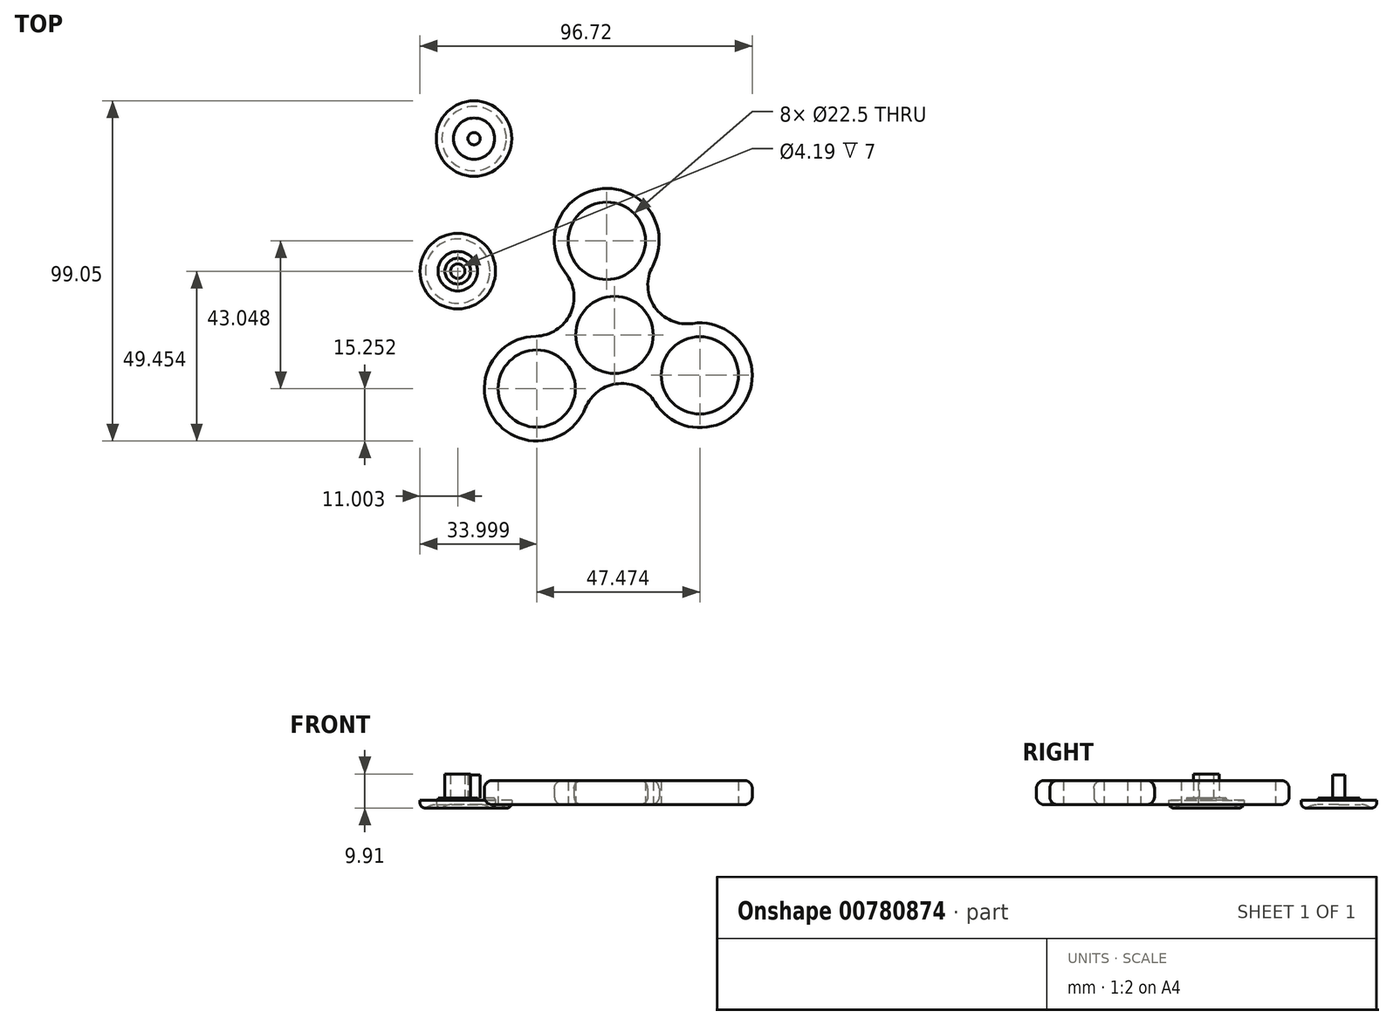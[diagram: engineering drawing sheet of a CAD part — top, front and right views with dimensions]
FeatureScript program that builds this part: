
annotation { "Feature Type Name" : "Feature", "Feature Type Description" : "" }
export const myFeature = defineFeature(function(context is Context, id is Id, definition is map)
    precondition{}
    {
        {
            var Q0;
            Q0=qCreatedBy(makeId("Top.planeOp"),FACE);
            var sketch = newSketch(context, id + "F0", { "sketchPlane" : qUnion([Q0])});
            skCircle(sketch, "E0", {"center": v(0, 0) * mm, "radius": 11.25 * mm});
            skCircle(sketch, "E1", {"center": v(-22.62, -15.64) * mm, "radius": 11.25 * mm});
            skCircle(sketch, "E2", {"center": v(24.85, -11.77) * mm, "radius": 11.25 * mm});
            skCircle(sketch, "E3", {"center": v(-2.23, 27.4) * mm, "radius": 11.25 * mm});
            skCircle(sketch, "E4.0", {"center": v(-22.62, -15.64) * mm, "radius": 15.25 * mm});
            skCircle(sketch, "E5.0", {"center": v(-2.23, 27.4) * mm, "radius": 15.25 * mm});
            skCircle(sketch, "E6.0", {"center": v(24.85, -11.77) * mm, "radius": 15.25 * mm});
            skLineSegment(sketch, "E7", {"start": v(-16.1, -1.86) * mm, "end": v(-8.76, 13.63) * mm, "construction": true});
            skLineSegment(sketch, "E8", {"start": v(16.18, 0.77) * mm, "end": v(6.44, 14.87) * mm, "construction": true});
            skLineSegment(sketch, "E9", {"start": v(-7.42, -14.4) * mm, "end": v(9.65, -13) * mm, "construction": true});
            skArc(sketch, "E10", {"start": v(11.8, -19.65) * mm, "mid": v(1.16, -14.2) * mm, "end": v(-8.46, -21.3) * mm});
            skArc(sketch, "E11", {"start": v(-22.92, -0.4) * mm, "mid": v(-12.88, 6.1) * mm, "end": v(-14.22, 17.98) * mm});
            skArc(sketch, "E12", {"start": v(11.12, 20.04) * mm, "mid": v(11.72, 8.1) * mm, "end": v(22.68, 3.32) * mm});
            skSolve(sketch);
        }
        {
            var Q0;
            Q0=makeQuery(id+"F0.imprint","IMPRINT",FACE,{"disambiguationData":[TD([[makeQuery(id+"F0.imprint","IMPRINT",EDGE,{"derivedFrom":sQuery(id+"F0.wireOp",EDGE,"E1")}),-1.0]])]});
            var Q1;
            Q1=makeQuery(id+"F0.imprint","IMPRINT",FACE,{"disambiguationData":[TD([[makeQuery(id+"F0.imprint","IMPRINT",EDGE,{"derivedFrom":sQuery(id+"F0.wireOp",EDGE,"E0")}),-1.0]])]});
            var Q2;
            Q2=makeQuery(id+"F0.imprint","IMPRINT",FACE,{"disambiguationData":[TD([[makeQuery(id+"F0.imprint","IMPRINT",EDGE,{"derivedFrom":sQuery(id+"F0.wireOp",EDGE,"E3")}),-1.0]])]});
            var Q3;
            Q3=makeQuery(id+"F0.imprint","IMPRINT",FACE,{"disambiguationData":[TD([[makeQuery(id+"F0.imprint","IMPRINT",EDGE,{"derivedFrom":sQuery(id+"F0.wireOp",EDGE,"E2")}),-1.0]])]});
            extrude(context, id + "F1", {"entities" : qUnion([Q0, Q1, Q2, Q3]), "depth" : 7 * mm, "offsetDistance" : 25.4 * mm});
        }
        {
            var Q0;
            Q0=makeQuery(id+"F1.opExtrude","CAP_EDGE",EDGE,{"disambiguationData":[OSD([sQuery(id+"F0.wireOp",EDGE,"E4.0")])],"isStart":false});
            fillet(context, id + "F2", {"entities" : qUnion([Q0]), "radius" : 2.3 * mm, "tangentPropagation" : true, "allowEdgeOverflow" : false});
        }
        {
            var Q0;
            Q0=makeQuery(id+"F1.opExtrude","CAP_EDGE",EDGE,{"disambiguationData":[OSD([sQuery(id+"F0.wireOp",EDGE,"E5.0")])],"isStart":true});
            fillet(context, id + "F3", {"entities" : qUnion([Q0]), "radius" : 2.3 * mm, "tangentPropagation" : true, "allowEdgeOverflow" : false});
        }
        {
            var Q0;
            Q0=qCreatedBy(makeId("Top.planeOp"),FACE);
            var sketch = newSketch(context, id + "F4", { "sketchPlane" : qUnion([Q0])});
            skCircle(sketch, "E13", {"center": v(-45.62, 18.56) * mm, "radius": 11 * mm});
            skCircle(sketch, "E14.0", {"center": v(-45.62, 18.56) * mm, "radius": 3.75 * mm});
            skCircle(sketch, "E15.0", {"center": v(-45.62, 18.56) * mm, "radius": 5.75 * mm});
            skCircle(sketch, "E16", {"center": v(-45.62, 18.56) * mm, "radius": 2.1 * mm});
            skSolve(sketch);
        }
        {
            var Q0;
            Q0=makeQuery(id+"F4.imprint","IMPRINT",FACE,{"disambiguationData":[TD([[makeQuery(id+"F4.imprint","IMPRINT",EDGE,{"derivedFrom":sQuery(id+"F4.wireOp",EDGE,"E13")}),1.0]])]});
            extrude(context, id + "F5", {"entities" : qUnion([Q0]), "depth" : 1.27 * mm, "offsetDistance" : 25.4 * mm});
        }
        {
            var Q0;
            Q0=makeQuery(id+"F4.imprint","IMPRINT",FACE,{"disambiguationData":[TD([[makeQuery(id+"F4.imprint","IMPRINT",EDGE,{"derivedFrom":sQuery(id+"F4.wireOp",EDGE,"E14.0")}),-1.0]])]});
            var Q1;
            Q1=makeQuery(id+"F4.imprint","IMPRINT",FACE,{"disambiguationData":[TD([[makeQuery(id+"F4.imprint","IMPRINT",EDGE,{"derivedFrom":sQuery(id+"F4.wireOp",EDGE,"E16")}),1.0]])]});
            extrude(context, id + "F6", {"entities" : qUnion([Q0, Q1]), "operationType" : NewBodyOperationType.ADD, "depth" : 1.9 * mm, "offsetDistance" : 25.4 * mm});
        }
        {
            var Q0;
            Q0=makeQuery(id+"F4.imprint","IMPRINT",FACE,{"disambiguationData":[TD([[makeQuery(id+"F4.imprint","IMPRINT",EDGE,{"derivedFrom":sQuery(id+"F4.wireOp",EDGE,"E14.0")}),1.0]])]});
            extrude(context, id + "F7", {"entities" : qUnion([Q0]), "operationType" : NewBodyOperationType.ADD, "depth" : 8.9 * mm, "offsetDistance" : 25.4 * mm});
        }
        {
            var Q0;
            Q0=qCreatedBy(makeId("Top.planeOp"),FACE);
            var sketch = newSketch(context, id + "F8", { "sketchPlane" : qUnion([Q0])});
            skCircle(sketch, "E17", {"center": v(-40.87, 57.16) * mm, "radius": 11 * mm});
            skCircle(sketch, "E18", {"center": v(-40.87, 57.16) * mm, "radius": 6 * mm});
            skCircle(sketch, "E19", {"center": v(-40.87, 57.16) * mm, "radius": 1.78 * mm});
            skSolve(sketch);
        }
        {
            var Q0;
            Q0=makeQuery(id+"F8.imprint","IMPRINT",FACE,{"disambiguationData":[TD([[makeQuery(id+"F8.imprint","IMPRINT",EDGE,{"derivedFrom":sQuery(id+"F8.wireOp",EDGE,"E17")}),1.0]])]});
            extrude(context, id + "F9", {"entities" : qUnion([Q0]), "depth" : 1.27 * mm, "offsetDistance" : 25.4 * mm});
        }
        {
            var Q0;
            Q0=makeQuery(id+"F8.imprint","IMPRINT",FACE,{"disambiguationData":[TD([[makeQuery(id+"F8.imprint","IMPRINT",EDGE,{"derivedFrom":sQuery(id+"F8.wireOp",EDGE,"E18")}),1.0]])]});
            extrude(context, id + "F10", {"entities" : qUnion([Q0]), "operationType" : NewBodyOperationType.ADD, "depth" : 1.9 * mm, "offsetDistance" : 25.4 * mm});
        }
        {
            var Q0;
            Q0=makeQuery(id+"F8.imprint","IMPRINT",FACE,{"disambiguationData":[TD([[makeQuery(id+"F8.imprint","IMPRINT",EDGE,{"derivedFrom":sQuery(id+"F8.wireOp",EDGE,"E19")}),1.0]])]});
            extrude(context, id + "F11", {"entities" : qUnion([Q0]), "operationType" : NewBodyOperationType.ADD, "depth" : 8.65 * mm, "offsetDistance" : 25.4 * mm});
        }
        {
            var Q0;
            Q0=makeQuery(id+"F8.imprint","IMPRINT",FACE,{"disambiguationData":[TD([[makeQuery(id+"F8.imprint","IMPRINT",EDGE,{"derivedFrom":sQuery(id+"F8.wireOp",EDGE,"E17")}),1.0]])]});
            var Q1;
            Q1=makeQuery(id+"F8.imprint","IMPRINT",FACE,{"disambiguationData":[TD([[makeQuery(id+"F8.imprint","IMPRINT",EDGE,{"derivedFrom":sQuery(id+"F8.wireOp",EDGE,"E18")}),1.0]])]});
            extrude(context, id + "F12", {"entities" : qUnion([Q0, Q1]), "operationType" : NewBodyOperationType.ADD, "oppositeDirection" : true, "depth" : 1 * mm, "offsetDistance" : 25.4 * mm});
        }
        {
            var Q0;
            Q0=makeQuery(id+"F12.opExtrude","CAP_FACE",FACE,{"disambiguationData":[OSD([sQuery(id+"F8.wireOp",EDGE,"E17"),sQuery(id+"F8.wireOp",EDGE,"E19")])],"isStart":false});
            var sketch = newSketch(context, id + "F13", { "sketchPlane" : qUnion([Q0])});
            skCircle(sketch, "E20", {"center": v(-40.87, -57.16) * mm, "radius": 9.36 * mm});
            skSolve(sketch);
        }
        {
            var Q0;
            Q0=makeQuery(id+"F13.imprint","IMPRINT",FACE,{"disambiguationData":[TD([[makeQuery(id+"F13.imprint","IMPRINT",EDGE,{"derivedFrom":sQuery(id+"F13.wireOp",EDGE,"E20")}),1.0]])]});
            extrude(context, id + "F14", {"entities" : qUnion([Q0]), "operationType" : NewBodyOperationType.REMOVE, "oppositeDirection" : true, "depth" : 1 * mm, "offsetDistance" : 25.4 * mm});
        }
        {
            var Q0;
            Q0=makeQuery(id+"F14.boolean.opBoolean","COPY",EDGE,{"derivedFrom":makeQuery(id+"F14.opExtrude","CAP_EDGE",EDGE,{"disambiguationData":[OSD([sQuery(id+"F13.wireOp",EDGE,"E20")])],"isStart":false})});
            fillet(context, id + "F15", {"entities" : qUnion([Q0]), "radius" : 5.08 * mm, "tangentPropagation" : true, "allowEdgeOverflow" : false});
        }
        {
            var Q0;
            Q0=makeQuery(id+"F12.opExtrude","CAP_EDGE",EDGE,{"disambiguationData":[OSD([sQuery(id+"F8.wireOp",EDGE,"E17")])],"isStart":false});
            fillet(context, id + "F16", {"entities" : qUnion([Q0]), "radius" : 1.5 * mm, "tangentPropagation" : true, "allowEdgeOverflow" : false});
        }
        {
            var Q0;
            Q0=makeQuery(id+"F4.imprint","IMPRINT",FACE,{"disambiguationData":[TD([[makeQuery(id+"F4.imprint","IMPRINT",EDGE,{"derivedFrom":sQuery(id+"F4.wireOp",EDGE,"E13")}),1.0]])]});
            var Q1;
            Q1=makeQuery(id+"F4.imprint","IMPRINT",FACE,{"disambiguationData":[TD([[makeQuery(id+"F4.imprint","IMPRINT",EDGE,{"derivedFrom":sQuery(id+"F4.wireOp",EDGE,"E14.0")}),-1.0]])]});
            var Q2;
            Q2=makeQuery(id+"F4.imprint","IMPRINT",FACE,{"disambiguationData":[TD([[makeQuery(id+"F4.imprint","IMPRINT",EDGE,{"derivedFrom":sQuery(id+"F4.wireOp",EDGE,"E16")}),1.0]])]});
            var Q3;
            Q3=makeQuery(id+"F4.imprint","IMPRINT",FACE,{"disambiguationData":[TD([[makeQuery(id+"F4.imprint","IMPRINT",EDGE,{"derivedFrom":sQuery(id+"F4.wireOp",EDGE,"E14.0")}),1.0]])]});
            extrude(context, id + "F17", {"entities" : qUnion([Q0, Q1, Q2, Q3]), "operationType" : NewBodyOperationType.ADD, "oppositeDirection" : true, "depth" : 1 * mm, "offsetDistance" : 25.4 * mm});
        }
        {
            var Q0;
            Q0=makeQuery(id+"F17.opExtrude","CAP_FACE",FACE,{"disambiguationData":[OSD([sQuery(id+"F4.wireOp",EDGE,"E13")])],"isStart":false});
            var sketch = newSketch(context, id + "F18", { "sketchPlane" : qUnion([Q0])});
            skCircle(sketch, "E21", {"center": v(-45.62, -18.56) * mm, "radius": 9.36 * mm});
            skSolve(sketch);
        }
        {
            var Q0;
            Q0=makeQuery(id+"F18.imprint","IMPRINT",FACE,{"disambiguationData":[TD([[makeQuery(id+"F18.imprint","IMPRINT",EDGE,{"derivedFrom":sQuery(id+"F18.wireOp",EDGE,"E21")}),1.0]])]});
            extrude(context, id + "F19", {"entities" : qUnion([Q0]), "operationType" : NewBodyOperationType.REMOVE, "oppositeDirection" : true, "depth" : 1 * mm, "offsetDistance" : 25.4 * mm});
        }
        {
            var Q0;
            Q0=makeQuery(id+"F19.boolean.opBoolean","COPY",EDGE,{"derivedFrom":makeQuery(id+"F19.opExtrude","CAP_EDGE",EDGE,{"disambiguationData":[OSD([sQuery(id+"F18.wireOp",EDGE,"E21")])],"isStart":false})});
            fillet(context, id + "F20", {"entities" : qUnion([Q0]), "radius" : 5.08 * mm, "tangentPropagation" : true, "allowEdgeOverflow" : false});
        }
        {
            var Q0;
            Q0=makeQuery(id+"F17.opExtrude","CAP_EDGE",EDGE,{"disambiguationData":[OSD([sQuery(id+"F4.wireOp",EDGE,"E13")])],"isStart":false});
            fillet(context, id + "F21", {"entities" : qUnion([Q0]), "radius" : 1.5 * mm, "tangentPropagation" : true, "allowEdgeOverflow" : false});
        }
    });
